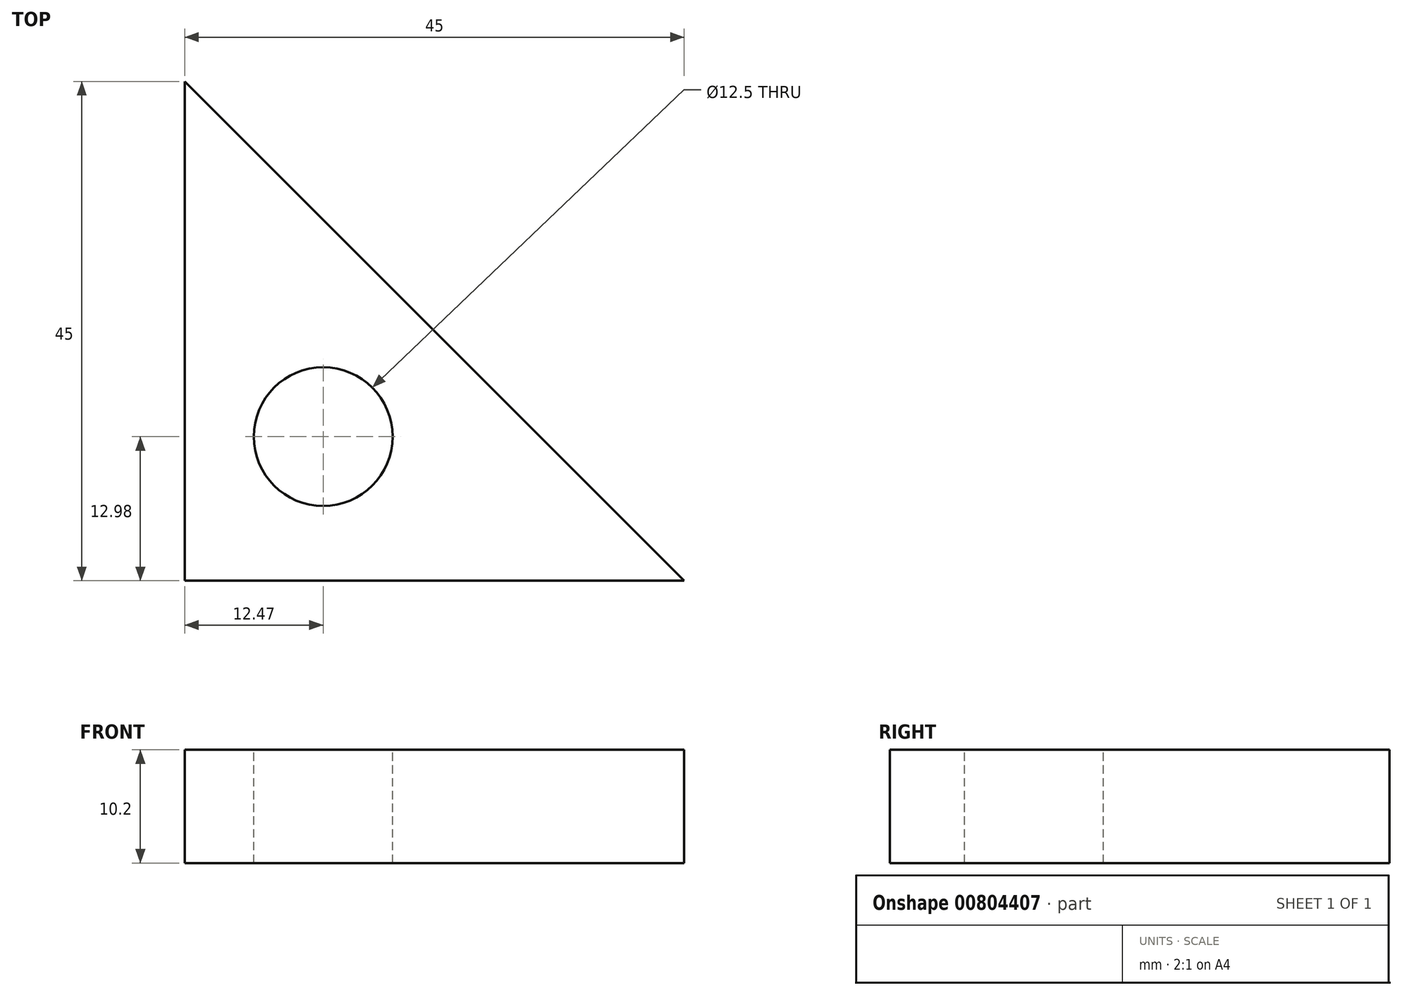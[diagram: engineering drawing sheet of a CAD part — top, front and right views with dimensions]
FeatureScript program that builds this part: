
annotation { "Feature Type Name" : "Feature", "Feature Type Description" : "" }
export const myFeature = defineFeature(function(context is Context, id is Id, definition is map)
    precondition{}
    {
        {
            var Q0;
            Q0=qCreatedBy(makeId("Top.planeOp"),FACE);
            var sketch = newSketch(context, id + "F0", { "sketchPlane" : qUnion([Q0])});
            skLineSegment(sketch, "E0", {"start": v(-12.47, -12.98) * mm, "end": v(32.53, -12.98) * mm});
            skLineSegment(sketch, "E1", {"start": v(-12.47, -12.98) * mm, "end": v(-12.47, 32.02) * mm});
            skLineSegment(sketch, "E2", {"start": v(-12.47, 32.02) * mm, "end": v(32.53, -12.98) * mm});
            skSolve(sketch);
        }
        {
            var Q0;
            Q0 = qSketchRegion(id + "F0", true);
            extrude(context, id + "F1", {"entities" : qUnion([Q0]), "depth" : 10.2 * mm, "offsetDistance" : 25.4 * mm});
        }
        {
            var Q0;
            Q0=makeQuery(id+"F1.opExtrude","CAP_FACE",FACE,{"disambiguationData":[OSD([sQuery(id+"F0.wireOp",EDGE,"E0"),sQuery(id+"F0.wireOp",EDGE,"E1"),sQuery(id+"F0.wireOp",EDGE,"E2")])],"isStart":false});
            var sketch = newSketch(context, id + "F2", { "sketchPlane" : qUnion([Q0])});
            skCircle(sketch, "E3", {"center": v(0, 0) * mm, "radius": 6.25 * mm});
            skSolve(sketch);
        }
        {
            var Q0;
            Q0 = qSketchRegion(id + "F2", true);
            extrude(context, id + "F3", {"entities" : qUnion([Q0]), "operationType" : NewBodyOperationType.REMOVE, "endBound" : BoundingType.THROUGH_ALL, "oppositeDirection" : true, "depth" : 2 * mm, "offsetDistance" : 25.4 * mm});
        }
    });
